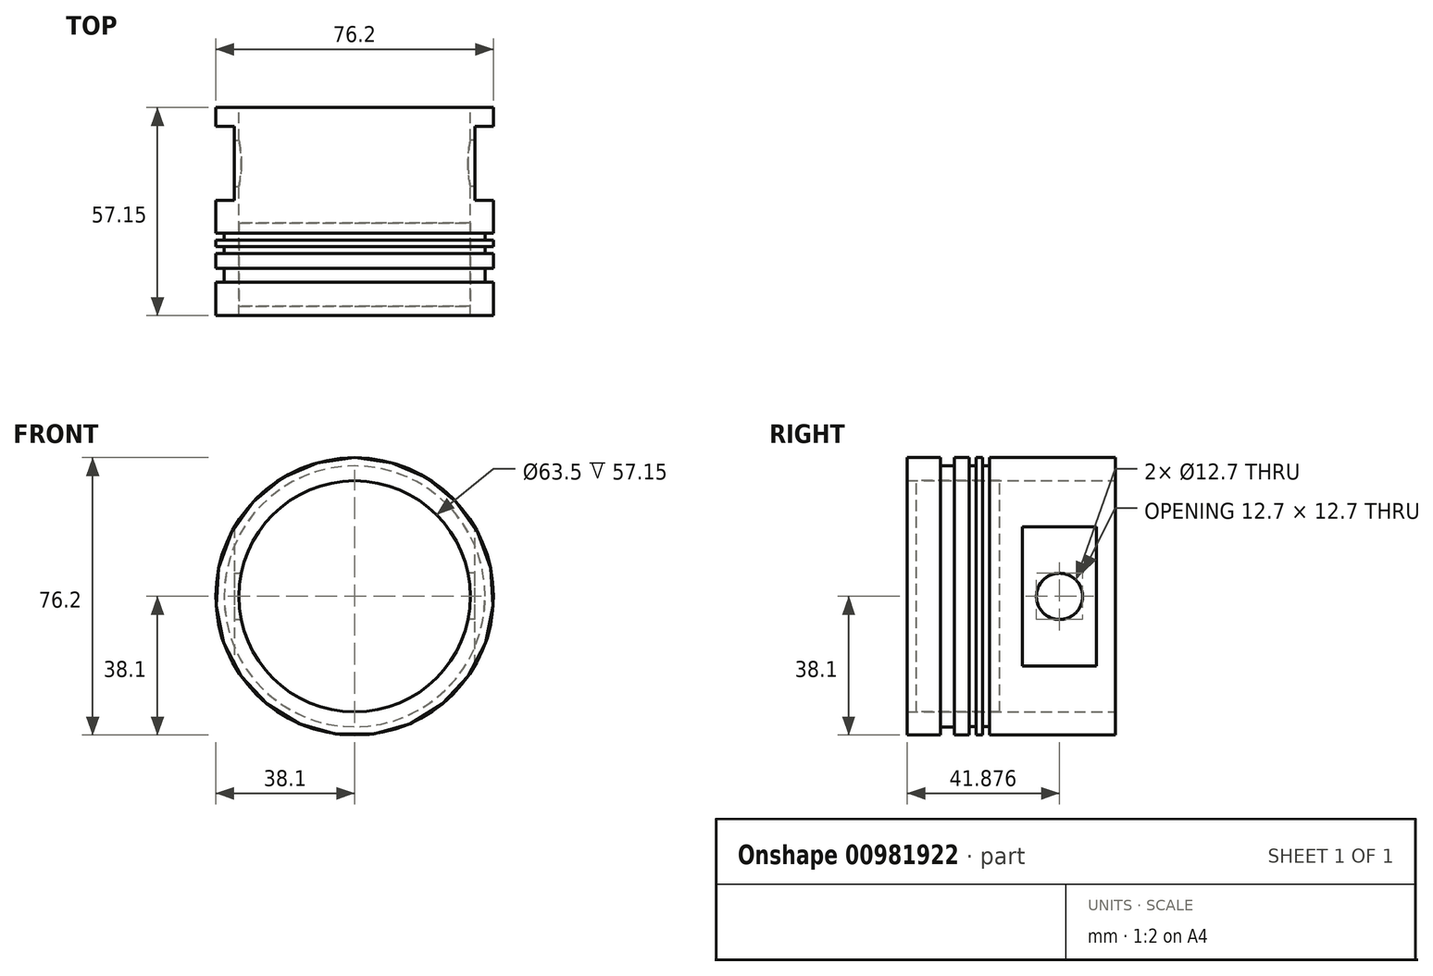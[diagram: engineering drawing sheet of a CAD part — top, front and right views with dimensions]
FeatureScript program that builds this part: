
annotation { "Feature Type Name" : "Feature", "Feature Type Description" : "" }
export const myFeature = defineFeature(function(context is Context, id is Id, definition is map)
    precondition{}
    {
        {
            var Q0;
            Q0=qCreatedBy(makeId("Front.planeOp"),FACE);
            var sketch = newSketch(context, id + "F0", { "sketchPlane" : qUnion([Q0])});
            skCircle(sketch, "E0", {"center": v(0, 0) * mm, "radius": 38.1 * mm});
            skCircle(sketch, "E1", {"center": v(0, 0) * mm, "radius": 31.75 * mm});
            skSolve(sketch);
        }
        {
            var Q0;
            Q0 = qSketchRegion(id + "F0", true);
            var Q1;
            Q1=makeQuery(id+"F0.imprint","IMPRINT",FACE,{"disambiguationData":[TD([[makeQuery(id+"F0.imprint","IMPRINT",EDGE,{"derivedFrom":sQuery(id+"F0.wireOp",EDGE,"E1")}),1.0]])]});
            extrude(context, id + "F1", {"entities" : qUnion([Q0, Q1]), "depth" : 63.5 * mm, "offsetDistance" : 25.4 * mm});
        }
        {
            var Q0;
            Q0=makeQuery(id+"F0.imprint","IMPRINT",FACE,{"disambiguationData":[TD([[makeQuery(id+"F0.imprint","IMPRINT",EDGE,{"derivedFrom":sQuery(id+"F0.wireOp",EDGE,"E1")}),1.0]])]});
            extrude(context, id + "F2", {"entities" : qUnion([Q0]), "operationType" : NewBodyOperationType.REMOVE, "oppositeDirection" : true, "depth" : 6.35 * mm, "offsetDistance" : 25.4 * mm});
        }
        {
            var Q0;
            Q0=makeQuery(id+"F0.imprint","IMPRINT",FACE,{"disambiguationData":[TD([[makeQuery(id+"F0.imprint","IMPRINT",EDGE,{"derivedFrom":sQuery(id+"F0.wireOp",EDGE,"E1")}),1.0]])]});
            extrude(context, id + "F3", {"entities" : qUnion([Q0]), "operationType" : NewBodyOperationType.REMOVE, "depth" : 6.35 * mm, "offsetDistance" : 25.4 * mm});
        }
        {
            var Q0;
            Q0=makeQuery(id+"F0.imprint","IMPRINT",FACE,{"disambiguationData":[TD([[makeQuery(id+"F0.imprint","IMPRINT",EDGE,{"derivedFrom":sQuery(id+"F0.wireOp",EDGE,"E0")}),1.0]])]});
            extrude(context, id + "F4", {"entities" : qUnion([Q0]), "operationType" : NewBodyOperationType.ADD, "oppositeDirection" : true, "depth" : 57.15 * mm, "offsetDistance" : 25.4 * mm});
        }
        {
            var Q0;
            Q0=makeQuery(id+"F1.opExtrude","CAP_FACE",FACE,{"disambiguationData":[OSD([sQuery(id+"F0.wireOp",EDGE,"E0")])],"isStart":false});
            extrude(context, id + "F5", {"entities" : qUnion([Q0]), "operationType" : NewBodyOperationType.REMOVE, "oppositeDirection" : true, "depth" : 63.5 * mm, "offsetDistance" : 25.4 * mm});
        }
        {
            var Q0;
            Q0=makeQuery(id+"F0.imprint","IMPRINT",FACE,{"disambiguationData":[TD([[makeQuery(id+"F0.imprint","IMPRINT",EDGE,{"derivedFrom":sQuery(id+"F0.wireOp",EDGE,"E1")}),1.0]])]});
            extrude(context, id + "F6", {"entities" : qUnion([Q0]), "oppositeDirection" : true, "depth" : 25.4 * mm, "offsetDistance" : 25.4 * mm});
        }
        {
            var Q0;
            Q0=makeQuery(id+"F0.imprint","IMPRINT",FACE,{"disambiguationData":[TD([[makeQuery(id+"F0.imprint","IMPRINT",EDGE,{"derivedFrom":sQuery(id+"F0.wireOp",EDGE,"E1")}),1.0]])]});
            extrude(context, id + "F7", {"entities" : qUnion([Q0]), "operationType" : NewBodyOperationType.REMOVE, "oppositeDirection" : true, "depth" : 2.54 * mm, "offsetDistance" : 25.4 * mm});
        }
        {
            var Q0;
            Q0=qCreatedBy(makeId("Right.planeOp"),FACE);
            var sketch = newSketch(context, id + "F8", { "sketchPlane" : qUnion([Q0])});
            skLineSegment(sketch, "E2.bottom", {"start": v(9.24, -38.36) * mm, "end": v(13.05, -38.36) * mm});
            skLineSegment(sketch, "E2.top", {"start": v(9.24, -35.82) * mm, "end": v(13.05, -35.82) * mm});
            skLineSegment(sketch, "E2.left", {"start": v(9.24, -38.36) * mm, "end": v(9.24, -35.82) * mm});
            skLineSegment(sketch, "E2.right", {"start": v(13.05, -38.36) * mm, "end": v(13.05, -35.82) * mm});
            skSolve(sketch);
        }
        {
            var Q0;
            Q0=makeQuery(id+"F8.imprint","IMPRINT",FACE,{"disambiguationData":[TD([[makeQuery(id+"F8.imprint","IMPRINT",EDGE,{"derivedFrom":sQuery(id+"F8.wireOp",EDGE,"E2.bottom")}),1.0]])]});
            var Q1;
            {var subQ0=sQuery(id+"F0.wireOp",EDGE,"E0");Q1=makeQuery(id+"F4.boolean.opBoolean","MERGE",FACE,{"derivedFrom":[makeQuery(id+"F1.opExtrude","SWEPT_FACE",FACE,{"disambiguationData":[OSD([subQ0])]}),makeQuery(id+"F4.opExtrude","SWEPT_FACE",FACE,{"disambiguationData":[OSD([subQ0])]})]});}
            revolve(context, id + "F9", {"operationType" : NewBodyOperationType.REMOVE, "surfaceOperationType" : NewSurfaceOperationType.NEW, "entities" : qUnion([Q0]), "axis" : qUnion([Q1]), "revolveType" : RevolveType.FULL, "oppositeDirection" : true});
        }
        {
            var Q0;
            Q0=qCreatedBy(makeId("Right.planeOp"),FACE);
            var sketch = newSketch(context, id + "F10", { "sketchPlane" : qUnion([Q0])});
            skLineSegment(sketch, "E3.bottom", {"start": v(17.03, -38.35) * mm, "end": v(18.94, -38.35) * mm});
            skLineSegment(sketch, "E3.top", {"start": v(17.03, -35.8) * mm, "end": v(18.94, -35.8) * mm});
            skLineSegment(sketch, "E3.left", {"start": v(17.03, -38.35) * mm, "end": v(17.03, -35.8) * mm});
            skLineSegment(sketch, "E3.right", {"start": v(18.94, -38.35) * mm, "end": v(18.94, -35.8) * mm});
            skSolve(sketch);
        }
        {
            var Q0;
            Q0=makeQuery(id+"F10.imprint","IMPRINT",FACE,{"disambiguationData":[TD([[makeQuery(id+"F10.imprint","IMPRINT",EDGE,{"derivedFrom":sQuery(id+"F10.wireOp",EDGE,"E3.bottom")}),1.0]])]});
            var Q1;
            {var subQ0=sQuery(id+"F0.wireOp",EDGE,"E0");Q1=makeQuery(id+"F9.boolean.opBoolean","SPLIT",FACE,{"disambiguationData":[TD([makeQuery(id+"F9.opRevolve","SWEPT_FACE",FACE,{"disambiguationData":[OSD([sQuery(id+"F8.wireOp",EDGE,"E2.right")])]})])],"derivedFrom":makeQuery(id+"F4.boolean.opBoolean","MERGE",FACE,{"derivedFrom":[makeQuery(id+"F1.opExtrude","SWEPT_FACE",FACE,{"disambiguationData":[OSD([subQ0])]}),makeQuery(id+"F4.opExtrude","SWEPT_FACE",FACE,{"disambiguationData":[OSD([subQ0])]})]})});}
            revolve(context, id + "F11", {"operationType" : NewBodyOperationType.REMOVE, "surfaceOperationType" : NewSurfaceOperationType.NEW, "entities" : qUnion([Q0]), "axis" : qUnion([Q1]), "revolveType" : RevolveType.FULL, "oppositeDirection" : true});
        }
        {
            var Q0;
            Q0=qCreatedBy(makeId("Right.planeOp"),FACE);
            var sketch = newSketch(context, id + "F12", { "sketchPlane" : qUnion([Q0])});
            skLineSegment(sketch, "E4", {"start": v(9.24, -38.1) * mm, "end": v(13.05, -38.1) * mm});
            skLineSegment(sketch, "E5", {"start": v(13.05, -38.1) * mm, "end": v(16.97, -38.1) * mm});
            skLineSegment(sketch, "E6", {"start": v(16.97, -38.1) * mm, "end": v(18.88, -38.1) * mm});
            skLineSegment(sketch, "E7", {"start": v(18.88, -38.1) * mm, "end": v(20.78, -38.1) * mm});
            skLineSegment(sketch, "E8.bottom", {"start": v(20.78, -38.1) * mm, "end": v(22.69, -38.1) * mm});
            skLineSegment(sketch, "E8.top", {"start": v(20.78, -35.82) * mm, "end": v(22.69, -35.82) * mm});
            skLineSegment(sketch, "E8.left", {"start": v(20.78, -38.1) * mm, "end": v(20.78, -35.82) * mm});
            skLineSegment(sketch, "E8.right", {"start": v(22.69, -38.1) * mm, "end": v(22.69, -35.82) * mm});
            skSolve(sketch);
        }
        {
            var Q0;
            Q0 = qSketchRegion(id + "F12", true);
            var Q1;
            {var subQ0=sQuery(id+"F0.wireOp",EDGE,"E0");Q1=makeQuery(id+"F11.boolean.opBoolean","SPLIT",FACE,{"disambiguationData":[TD([makeQuery(id+"F11.opRevolve","SWEPT_FACE",FACE,{"disambiguationData":[OSD([sQuery(id+"F10.wireOp",EDGE,"E3.right")])]})])],"derivedFrom":makeQuery(id+"F9.boolean.opBoolean","SPLIT",FACE,{"disambiguationData":[TD([makeQuery(id+"F9.opRevolve","SWEPT_FACE",FACE,{"disambiguationData":[OSD([sQuery(id+"F8.wireOp",EDGE,"E2.right")])]})])],"derivedFrom":makeQuery(id+"F4.boolean.opBoolean","MERGE",FACE,{"derivedFrom":[makeQuery(id+"F1.opExtrude","SWEPT_FACE",FACE,{"disambiguationData":[OSD([subQ0])]}),makeQuery(id+"F4.opExtrude","SWEPT_FACE",FACE,{"disambiguationData":[OSD([subQ0])]})]})})});}
            revolve(context, id + "F13", {"operationType" : NewBodyOperationType.REMOVE, "surfaceOperationType" : NewSurfaceOperationType.NEW, "entities" : qUnion([Q0]), "axis" : qUnion([Q1]), "revolveType" : RevolveType.FULL, "oppositeDirection" : true});
        }
        {
            var Q0;
            Q0=qCreatedBy(makeId("Top.planeOp"),FACE);
            var sketch = newSketch(context, id + "F14", { "sketchPlane" : qUnion([Q0])});
            skLineSegment(sketch, "E9.bottom", {"start": v(-40.6, 31.72) * mm, "end": v(-32.98, 31.72) * mm});
            skLineSegment(sketch, "E9.top", {"start": v(-40.6, 52.04) * mm, "end": v(-32.98, 52.04) * mm});
            skLineSegment(sketch, "E9.left", {"start": v(-40.6, 31.72) * mm, "end": v(-40.6, 52.04) * mm});
            skLineSegment(sketch, "E9.right", {"start": v(-32.98, 31.72) * mm, "end": v(-32.98, 52.04) * mm});
            skLineSegment(sketch, "E10.MirrorCS", {"start": v(40.6, 31.72) * mm, "end": v(40.6, 52.04) * mm});
            skLineSegment(sketch, "E11.MirrorCS", {"start": v(40.6, 52.04) * mm, "end": v(32.98, 52.04) * mm});
            skLineSegment(sketch, "E12.MirrorCS", {"start": v(32.98, 31.72) * mm, "end": v(32.98, 52.04) * mm});
            skLineSegment(sketch, "E13.MirrorCS", {"start": v(40.6, 31.72) * mm, "end": v(32.98, 31.72) * mm});
            skSolve(sketch);
        }
        {
            var Q0;
            Q0=makeQuery(id+"F14.imprint","IMPRINT",FACE,{"disambiguationData":[TD([[makeQuery(id+"F14.imprint","IMPRINT",EDGE,{"derivedFrom":sQuery(id+"F14.wireOp",EDGE,"E9.bottom")}),1.0]])]});
            extrude(context, id + "F15", {"entities" : qUnion([Q0]), "operationType" : NewBodyOperationType.REMOVE, "depth" : 50.8 * mm, "offsetDistance" : 25.4 * mm, "hasSecondDirection" : true, "secondDirectionOppositeDirection" : true, "secondDirectionDepth" : 50.8 * mm});
        }
        {
            var Q0;
            Q0=makeQuery(id+"F14.imprint","IMPRINT",FACE,{"disambiguationData":[TD([[makeQuery(id+"F14.imprint","IMPRINT",EDGE,{"derivedFrom":sQuery(id+"F14.wireOp",EDGE,"E10.MirrorCS")}),1.0]])]});
            extrude(context, id + "F16", {"entities" : qUnion([Q0]), "operationType" : NewBodyOperationType.REMOVE, "oppositeDirection" : true, "depth" : 50.8 * mm, "offsetDistance" : 25.4 * mm, "hasSecondDirection" : true, "secondDirectionOppositeDirection" : false, "secondDirectionDepth" : 50.8 * mm});
        }
        {
            var Q0;
            Q0=qCreatedBy(makeId("Right.planeOp"),FACE);
            var sketch = newSketch(context, id + "F17", { "sketchPlane" : qUnion([Q0])});
            skPoint(sketch, "E14", {"position": v(41.88, 0) * mm});
            skSolve(sketch);
        }
        {
            var Q0;
            Q0=sQuery(id+"F17.wireOp",VERTEX,"E14");
            var Q1;
            Q1=makeQuery(id+"F1.opExtrude","SWEPT_BODY",BODY,{"disambiguationData":[OSD([sQuery(id+"F0.wireOp",EDGE,"E0")])]});
            hole(context, id + "F18", {"style" : HoleStyle.SIMPLE, "endStyle" : HoleEndStyle.BLIND, "holeDiameter" : 12.7 * mm, "majorDiameter" : 6.35 * mm, "holeDepth" : 127 * mm, "isTappedThrough" : true, "tappedDepth" : 12.7 * mm, "tapClearance" : 3, "startFromSketch" : true, "locations" : qUnion([Q0]), "scope" : qUnion([Q1])});
        }
        {
            var Q0;
            Q0=sQuery(id+"F17.wireOp",VERTEX,"E14");
            var Q1;
            Q1=makeQuery(id+"F1.opExtrude","SWEPT_BODY",BODY,{"disambiguationData":[OSD([sQuery(id+"F0.wireOp",EDGE,"E0")])]});
            hole(context, id + "F19", {"style" : HoleStyle.SIMPLE, "endStyle" : HoleEndStyle.BLIND, "oppositeDirection" : true, "holeDiameter" : 12.7 * mm, "majorDiameter" : 6.35 * mm, "holeDepth" : 127 * mm, "isTappedThrough" : true, "tappedDepth" : 12.7 * mm, "tapClearance" : 3, "startFromSketch" : true, "locations" : qUnion([Q0]), "scope" : qUnion([Q1])});
        }
    });
